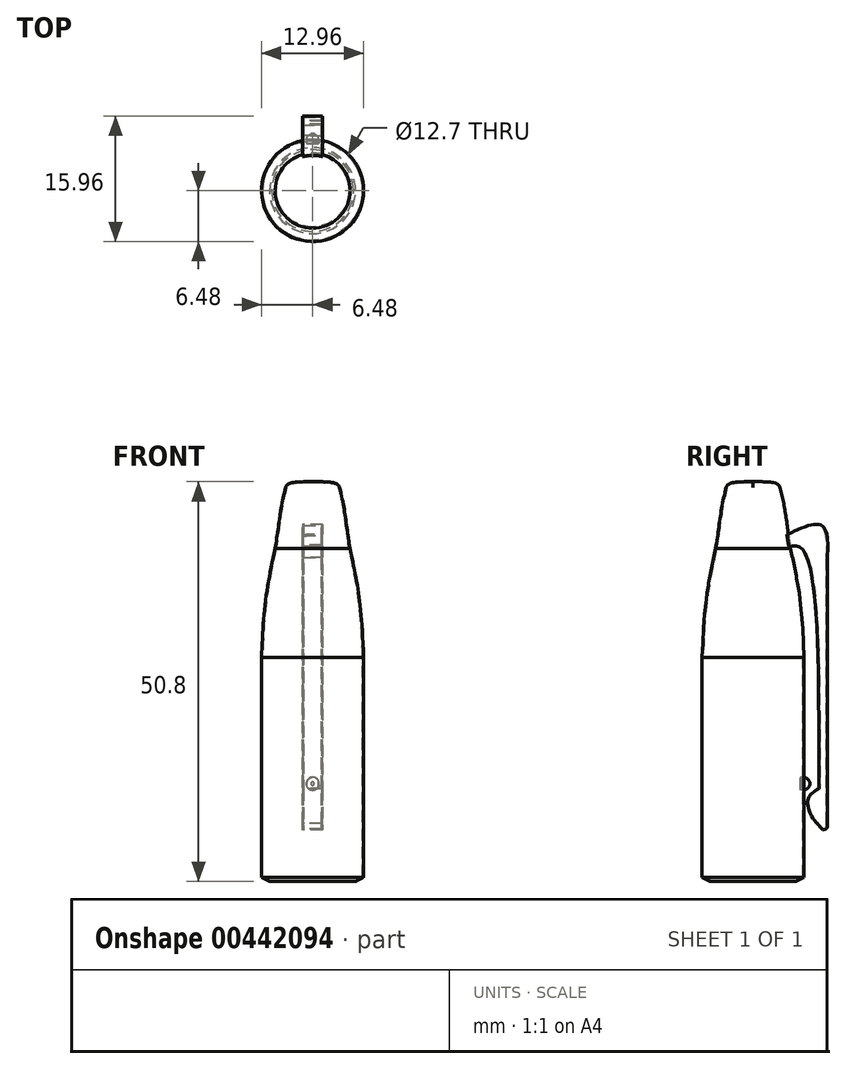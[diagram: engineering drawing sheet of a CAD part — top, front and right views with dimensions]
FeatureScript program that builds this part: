
annotation { "Feature Type Name" : "Feature", "Feature Type Description" : "" }
export const myFeature = defineFeature(function(context is Context, id is Id, definition is map)
    precondition{}
    {
        {
            var Q0;
            Q0=qCreatedBy(makeId("Front.planeOp"),FACE);
            var sketch = newSketch(context, id + "F0", { "sketchPlane" : qUnion([Q0])});
            skLineSegment(sketch, "E0", {"start": v(-22.13, 50.8) * mm, "end": v(38.53, 50.8) * mm, "construction": true});
            skLineSegment(sketch, "E1", {"start": v(6.48, 57.61) * mm, "end": v(6.48, -6.81) * mm, "construction": true});
            skLineSegment(sketch, "E2", {"start": v(-7.17, 28.45) * mm, "end": v(21.94, 28.45) * mm, "construction": true});
            skLineSegment(sketch, "E3", {"start": v(-7.06, 42.3) * mm, "end": v(23.04, 42.3) * mm, "construction": true});
            skLineSegment(sketch, "E4", {"start": v(4.76, 58.76) * mm, "end": v(4.76, -11.65) * mm, "construction": true});
            skLineSegment(sketch, "E5", {"start": v(0, 0) * mm, "end": v(5.46, 0) * mm});
            skFitSpline(sketch, "E6", {"points": [v(5.46, 0) * mm, v(6.48, 0.55) * mm], "startDerivative": vector(1.02, 0.55) * mm, "endDerivative": vector(1.02, 0.55) * mm});
            skLineSegment(sketch, "E7", {"start": v(6.48, 0.55) * mm, "end": v(6.48, 28.45) * mm});
            skFitSpline(sketch, "E8", {"points": [v(6.48, 28.45) * mm, v(4.76, 42.3) * mm], "startDerivative": vector(-0.76, 22.2) * mm, "endDerivative": vector(-2.83, 13.7) * mm});
            skLineSegment(sketch, "E9", {"start": v(3.43, 61.41) * mm, "end": v(3.43, -2.08) * mm, "construction": true});
            skFitSpline(sketch, "E10", {"points": [v(0, 50.8) * mm, v(3.43, 50.08) * mm], "startDerivative": vector(6.34, 0) * mm, "endDerivative": vector(0.53, -2.16) * mm});
            skFitSpline(sketch, "E11", {"points": [v(4.76, 42.3) * mm, v(3.43, 50.08) * mm], "startDerivative": vector(-1.33, 7.8) * mm, "endDerivative": vector(-2.23, 8.7) * mm});
            skLineSegment(sketch, "E12", {"start": v(0, 50.8) * mm, "end": v(0, 0) * mm});
            skSolve(sketch);
        }
        {
            var Q0;
            Q0=qSketchRegion(id+"F0",true);
            var Q1;
            Q1=sQuery(id+"F0.wireOp",EDGE,"E12");
            revolve(context, id + "F1", {"entities" : qUnion([Q0]), "axis" : qUnion([Q1]), "revolveType" : RevolveType.FULL});
        }
        {
            var Q0;
            Q0=qCreatedBy(makeId("Right.planeOp"),FACE);
            var sketch = newSketch(context, id + "F2", { "sketchPlane" : qUnion([Q0])});
            skFitSpline(sketch, "E13", {"points": [v(3.81, 42.3) * mm, v(6.22, 42.27) * mm, v(8.35, 11.81) * mm], "startDerivative": vector(10.38, 3.24) * mm, "endDerivative": vector(0.34, -38.61) * mm});
            skFitSpline(sketch, "E14", {"points": [v(8.35, 11.81) * mm, v(7.12, 10.83) * mm, v(7.02, 9.28) * mm, v(8.83, 6.59) * mm], "startDerivative": vector(-5.12, -3.04) * mm, "endDerivative": vector(7.2, -7) * mm});
            skFitSpline(sketch, "E15", {"points": [v(8.83, 6.59) * mm, v(9.45, 7.37) * mm], "startDerivative": vector(1.78, 0.13) * mm, "endDerivative": vector(-0.04, 1.66) * mm});
            skFitSpline(sketch, "E16", {"points": [v(9.45, 7.37) * mm, v(9.45, 41.15) * mm], "startDerivative": vector(0, 33.78) * mm, "endDerivative": vector(0, 33.78) * mm});
            skPoint(sketch, "E17.end.orphan", {"position": v(9.45, 44.96) * mm});
            skFitSpline(sketch, "E18", {"points": [v(9.45, 41.15) * mm, v(8.73, 45.22) * mm, v(3.67, 43.75) * mm], "startDerivative": vector(0.36, 11.35) * mm, "endDerivative": vector(-11.67, -5.8) * mm});
            skLineSegment(sketch, "E19", {"start": v(3.81, 42.3) * mm, "end": v(3.67, 43.75) * mm});
            skSolve(sketch);
        }
        {
            var Q0;
            Q0=qSketchRegion(id+"F2",true);
            extrude(context, id + "F3", {"entities" : qUnion([Q0]), "operationType" : NewBodyOperationType.ADD, "depth" : 1.27 * mm, "hasSecondDirection" : true, "secondDirectionOppositeDirection" : true, "secondDirectionDepth" : 1.27 * mm});
        }
        {
            var Q0;
            Q0=makeQuery(id+"F1.opRevolve","SWEPT_FACE",FACE,{"disambiguationData":[OSD([sQuery(id+"F0.wireOp",EDGE,"E5")])]});
            shell(context, id + "F4", {"entities" : qUnion([Q0]), "thickness" : 0.13 * mm});
        }
        {
            var Q0;
            Q0=qCreatedBy(makeId("Right.planeOp"),FACE);
            var sketch = newSketch(context, id + "F5", { "sketchPlane" : qUnion([Q0])});
            skLineSegment(sketch, "E20", {"start": v(6, 12.43) * mm, "end": v(7.23, 12.43) * mm});
            skLineSegment(sketch, "E21", {"start": v(6, 12.43) * mm, "end": v(6, 11.66) * mm});
            skArc(sketch, "E22", {"start": v(6, 11.66) * mm, "mid": v(6.8, 11.75) * mm, "end": v(7.23, 12.43) * mm});
            skSolve(sketch);
        }
        {
            var Q0;
            Q0=qSketchRegion(id+"F5",true);
            var Q1;
            Q1=sQuery(id+"F5.wireOp",EDGE,"E20");
            revolve(context, id + "F6", {"operationType" : NewBodyOperationType.ADD, "entities" : qUnion([Q0]), "axis" : qUnion([Q1]), "revolveType" : RevolveType.FULL});
        }
    });
